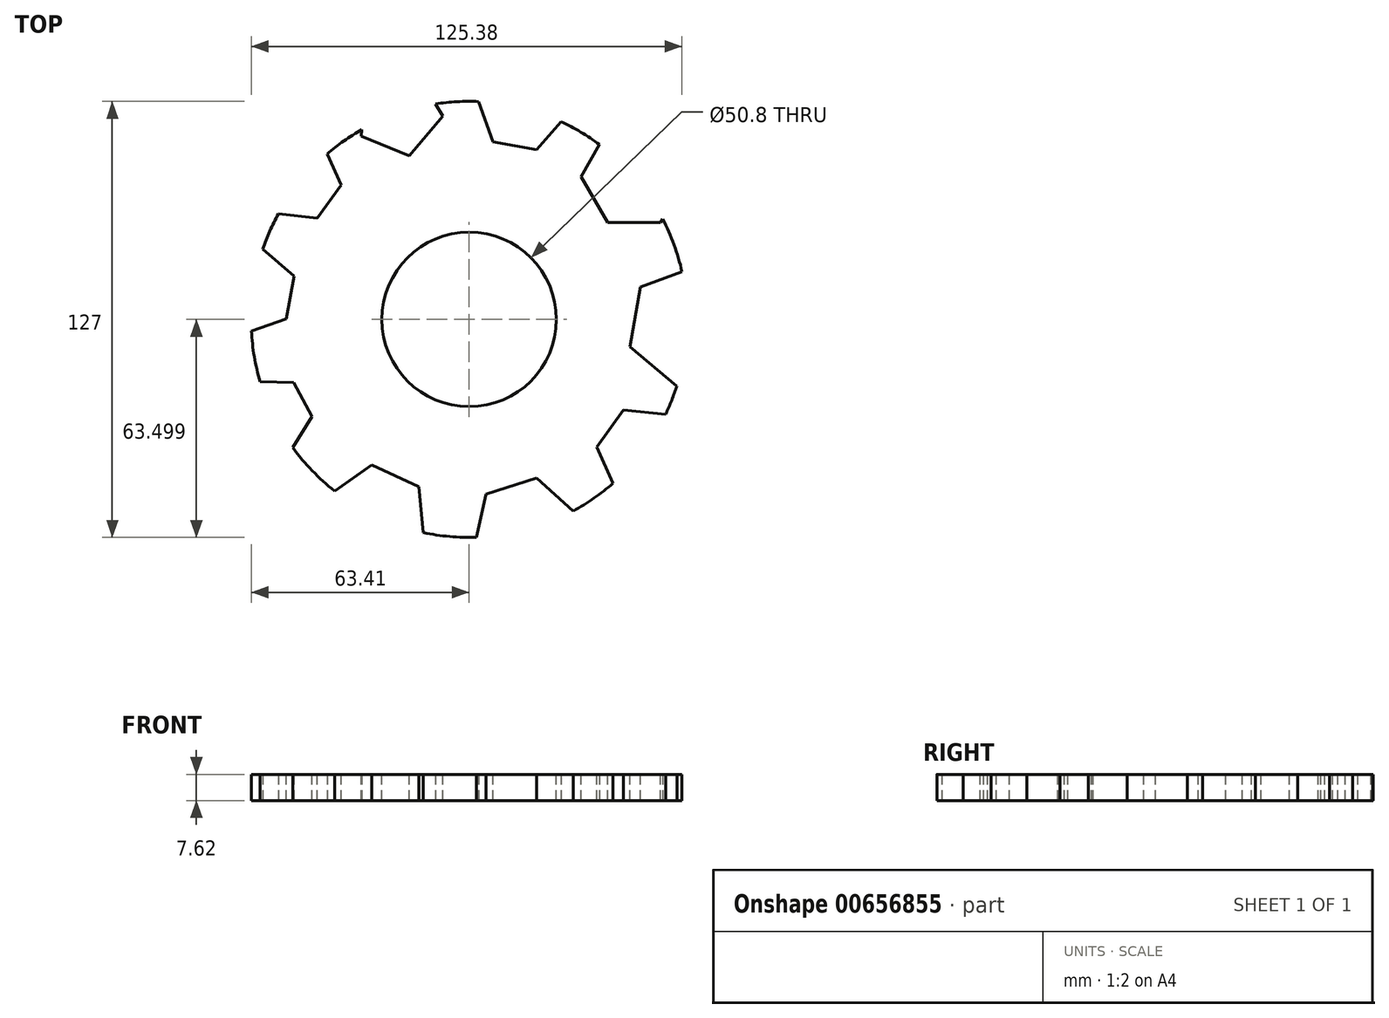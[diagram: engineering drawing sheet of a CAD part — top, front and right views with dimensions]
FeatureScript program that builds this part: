
annotation { "Feature Type Name" : "Feature", "Feature Type Description" : "" }
export const myFeature = defineFeature(function(context is Context, id is Id, definition is map)
    precondition{}
    {
        {
            var Q0;
            Q0=qCreatedBy(makeId("Top.planeOp"),FACE);
            var sketch = newSketch(context, id + "F0", { "sketchPlane" : qUnion([Q0])});
            skCircle(sketch, "E0", {"center": v(-7.68, 7.64) * mm, "radius": 63.5 * mm});
            skSolve(sketch);
        }
        {
            var Q0;
            Q0=makeQuery(id+"F0.imprint","IMPRINT",FACE,{"disambiguationData":[TD([[makeQuery(id+"F0.imprint","IMPRINT",EDGE,{"derivedFrom":sQuery(id+"F0.wireOp",EDGE,"E0")}),1.0]])]});
            extrude(context, id + "F1", {"entities" : qUnion([Q0]), "depth" : 7.62 * mm, "offsetDistance" : 25.4 * mm});
        }
        {
            var Q0;
            Q0=makeQuery(id+"F1.opExtrude","CAP_FACE",FACE,{"disambiguationData":[OSD([sQuery(id+"F0.wireOp",EDGE,"E0")])],"isStart":false});
            var sketch = newSketch(context, id + "F2", { "sketchPlane" : qUnion([Q0])});
            skCircle(sketch, "E1", {"center": v(-7.68, 7.64) * mm, "radius": 25.4 * mm});
            skSolve(sketch);
        }
        {
            var Q0;
            Q0 = qSketchRegion(id + "F2", true);
            extrude(context, id + "F3", {"entities" : qUnion([Q0]), "operationType" : NewBodyOperationType.REMOVE, "oppositeDirection" : true, "depth" : 10.16 * mm, "offsetDistance" : 25.4 * mm});
        }
        {
            var Q0;
            Q0=makeQuery(id+"F1.opExtrude","CAP_FACE",FACE,{"disambiguationData":[OSD([sQuery(id+"F0.wireOp",EDGE,"E0")])],"isStart":false});
            var sketch = newSketch(context, id + "F4", { "sketchPlane" : qUnion([Q0])});
            skCircle(sketch, "E2.cCircle", {"center": v(-64.68, -20.34) * mm, "radius": 11.21 * mm, "construction": true});
            skLineSegment(sketch, "E2.0", {"start": v(-75.9, -20.03) * mm, "end": v(-70.02, -10.47) * mm});
            skLineSegment(sketch, "E2.1", {"start": v(-70.02, -10.47) * mm, "end": v(-58.8, -10.79) * mm});
            skLineSegment(sketch, "E2.2", {"start": v(-58.8, -10.79) * mm, "end": v(-53.47, -20.65) * mm});
            skLineSegment(sketch, "E2.3", {"start": v(-53.47, -20.65) * mm, "end": v(-59.35, -30.2) * mm});
            skLineSegment(sketch, "E2.4", {"start": v(-59.35, -30.2) * mm, "end": v(-70.56, -29.9) * mm});
            skLineSegment(sketch, "E2.5", {"start": v(-70.56, -29.9) * mm, "end": v(-75.9, -20.03) * mm});
            skCircle(sketch, "E3.cCircle", {"center": v(-70.61, 16.1) * mm, "radius": 12.67 * mm, "construction": true});
            skLineSegment(sketch, "E3.0", {"start": v(-61, 7.85) * mm, "end": v(-72.94, 3.64) * mm});
            skLineSegment(sketch, "E3.1", {"start": v(-72.94, 3.64) * mm, "end": v(-82.56, 11.88) * mm});
            skLineSegment(sketch, "E3.2", {"start": v(-82.56, 11.88) * mm, "end": v(-80.24, 24.33) * mm});
            skLineSegment(sketch, "E3.3", {"start": v(-80.24, 24.33) * mm, "end": v(-68.29, 28.54) * mm});
            skLineSegment(sketch, "E3.4", {"start": v(-68.29, 28.54) * mm, "end": v(-58.67, 20.3) * mm});
            skLineSegment(sketch, "E3.5", {"start": v(-58.67, 20.3) * mm, "end": v(-61, 7.85) * mm});
            skCircle(sketch, "E4.cCircle", {"center": v(-56.72, 47.97) * mm, "radius": 11.81 * mm, "construction": true});
            skLineSegment(sketch, "E4.0", {"start": v(-51.91, 37.19) * mm, "end": v(-63.66, 38.41) * mm});
            skLineSegment(sketch, "E4.1", {"start": v(-63.66, 38.41) * mm, "end": v(-68.47, 49.2) * mm});
            skLineSegment(sketch, "E4.2", {"start": v(-68.47, 49.2) * mm, "end": v(-61.54, 58.76) * mm});
            skLineSegment(sketch, "E4.3", {"start": v(-61.54, 58.76) * mm, "end": v(-49.79, 57.54) * mm});
            skLineSegment(sketch, "E4.4", {"start": v(-49.79, 57.54) * mm, "end": v(-44.98, 46.75) * mm});
            skLineSegment(sketch, "E4.5", {"start": v(-44.98, 46.75) * mm, "end": v(-51.91, 37.19) * mm});
            skCircle(sketch, "E5.cCircle", {"center": v(-28.15, 67.75) * mm, "radius": 12.87 * mm, "construction": true});
            skLineSegment(sketch, "E5.0", {"start": v(-37.98, 76.05) * mm, "end": v(-23.3, 79.66) * mm});
            skLineSegment(sketch, "E5.1", {"start": v(-23.3, 79.66) * mm, "end": v(-15.32, 66.81) * mm});
            skLineSegment(sketch, "E5.2", {"start": v(-15.32, 66.81) * mm, "end": v(-25.08, 55.25) * mm});
            skLineSegment(sketch, "E5.3", {"start": v(-25.08, 55.25) * mm, "end": v(-39.08, 60.96) * mm});
            skLineSegment(sketch, "E5.4", {"start": v(-39.08, 60.96) * mm, "end": v(-37.98, 76.05) * mm});
            skCircle(sketch, "E6.cCircle", {"center": v(-34.7, -49.83) * mm, "radius": 15.18 * mm, "construction": true});
            skLineSegment(sketch, "E6.0", {"start": v(-33.29, -64.94) * mm, "end": v(-47.08, -58.6) * mm});
            skLineSegment(sketch, "E6.1", {"start": v(-47.08, -58.6) * mm, "end": v(-48.5, -43.5) * mm});
            skLineSegment(sketch, "E6.2", {"start": v(-48.5, -43.5) * mm, "end": v(-36.11, -34.71) * mm});
            skLineSegment(sketch, "E6.3", {"start": v(-36.11, -34.71) * mm, "end": v(-22.32, -41.04) * mm});
            skLineSegment(sketch, "E6.4", {"start": v(-22.32, -41.04) * mm, "end": v(-20.9, -56.16) * mm});
            skLineSegment(sketch, "E6.5", {"start": v(-20.9, -56.16) * mm, "end": v(-33.29, -64.94) * mm});
            skCircle(sketch, "E7.cCircle", {"center": v(8.66, -53.72) * mm, "radius": 15.54 * mm, "construction": true});
            skLineSegment(sketch, "E7.0", {"start": v(20.16, -64.18) * mm, "end": v(5.36, -68.9) * mm});
            skLineSegment(sketch, "E7.1", {"start": v(5.36, -68.9) * mm, "end": v(-6.14, -58.45) * mm});
            skLineSegment(sketch, "E7.2", {"start": v(-6.14, -58.45) * mm, "end": v(-2.83, -43.26) * mm});
            skLineSegment(sketch, "E7.3", {"start": v(-2.83, -43.26) * mm, "end": v(11.97, -38.53) * mm});
            skLineSegment(sketch, "E7.4", {"start": v(11.97, -38.53) * mm, "end": v(23.47, -49) * mm});
            skLineSegment(sketch, "E7.5", {"start": v(23.47, -49) * mm, "end": v(20.16, -64.18) * mm});
            skCircle(sketch, "E8.cCircle", {"center": v(42.78, -30.91) * mm, "radius": 13.37 * mm, "construction": true});
            skLineSegment(sketch, "E8.0", {"start": v(48.28, -43.1) * mm, "end": v(34.98, -41.77) * mm});
            skLineSegment(sketch, "E8.1", {"start": v(34.98, -41.77) * mm, "end": v(29.48, -29.59) * mm});
            skLineSegment(sketch, "E8.2", {"start": v(29.48, -29.59) * mm, "end": v(37.28, -18.73) * mm});
            skLineSegment(sketch, "E8.3", {"start": v(37.28, -18.73) * mm, "end": v(50.58, -20.06) * mm});
            skLineSegment(sketch, "E8.4", {"start": v(50.58, -20.06) * mm, "end": v(56.08, -32.24) * mm});
            skLineSegment(sketch, "E8.5", {"start": v(56.08, -32.24) * mm, "end": v(48.28, -43.1) * mm});
            skCircle(sketch, "E9.cCircle", {"center": v(55.8, 5.7) * mm, "radius": 17.73 * mm, "construction": true});
            skLineSegment(sketch, "E9.0", {"start": v(69.4, -5.66) * mm, "end": v(52.75, -11.75) * mm});
            skLineSegment(sketch, "E9.1", {"start": v(52.75, -11.75) * mm, "end": v(39.15, -0.38) * mm});
            skLineSegment(sketch, "E9.2", {"start": v(39.15, -0.38) * mm, "end": v(42.2, 17.08) * mm});
            skLineSegment(sketch, "E9.3", {"start": v(42.2, 17.08) * mm, "end": v(58.84, 23.17) * mm});
            skLineSegment(sketch, "E9.4", {"start": v(58.84, 23.17) * mm, "end": v(72.44, 11.8) * mm});
            skLineSegment(sketch, "E9.5", {"start": v(72.44, 11.8) * mm, "end": v(69.4, -5.66) * mm});
            skCircle(sketch, "E10.cCircle", {"center": v(40.33, 49.2) * mm, "radius": 15.46 * mm, "construction": true});
            skLineSegment(sketch, "E10.0", {"start": v(55.79, 49.2) * mm, "end": v(48.06, 35.81) * mm});
            skLineSegment(sketch, "E10.1", {"start": v(48.06, 35.81) * mm, "end": v(32.6, 35.81) * mm});
            skLineSegment(sketch, "E10.2", {"start": v(32.6, 35.81) * mm, "end": v(24.87, 49.2) * mm});
            skLineSegment(sketch, "E10.3", {"start": v(24.87, 49.2) * mm, "end": v(32.6, 62.59) * mm});
            skLineSegment(sketch, "E10.4", {"start": v(32.6, 62.59) * mm, "end": v(48.06, 62.59) * mm});
            skLineSegment(sketch, "E10.5", {"start": v(48.06, 62.59) * mm, "end": v(55.79, 49.2) * mm});
            skCircle(sketch, "E11.cCircle", {"center": v(7.66, 69.26) * mm, "radius": 12.96 * mm, "construction": true});
            skLineSegment(sketch, "E11.0", {"start": v(16.08, 79.1) * mm, "end": v(20.4, 66.88) * mm});
            skLineSegment(sketch, "E11.1", {"start": v(20.4, 66.88) * mm, "end": v(11.97, 57.04) * mm});
            skLineSegment(sketch, "E11.2", {"start": v(11.97, 57.04) * mm, "end": v(-0.77, 59.41) * mm});
            skLineSegment(sketch, "E11.3", {"start": v(-0.77, 59.41) * mm, "end": v(-5.09, 71.63) * mm});
            skLineSegment(sketch, "E11.4", {"start": v(-5.09, 71.63) * mm, "end": v(3.34, 81.48) * mm});
            skLineSegment(sketch, "E11.5", {"start": v(3.34, 81.48) * mm, "end": v(16.08, 79.1) * mm});
            skSolve(sketch);
        }
        {
            var Q0;
            Q0 = qSketchRegion(id + "F4", true);
            extrude(context, id + "F5", {"entities" : qUnion([Q0]), "operationType" : NewBodyOperationType.REMOVE, "oppositeDirection" : true, "depth" : 25.4 * mm, "offsetDistance" : 25.4 * mm});
        }
    });
